# Revit family: KFL2
name_source: partatom
category: Lighting Fixtures
revit_build: Autodesk Revit 2014 (Build: 20130308_1515(x64)
units: mm (PartAtom-declared; Revit-internal decimal feet)

## types (1)
- KFL2-11L-35-RGBWW-MF-UNV-K-WH-DMX-WM
    Apparent Load = 35 VA
    Application = Flood Lighting,Sign Lighting,Landscape Lighting,Facade Lighting,Flag Pole Lighting,Sculpture Lighting,Monuments Lighting,Grazing Lighting,Washing Lighting,Column Lighting,Canopy Lighting
    Assembly Code = D5020200
    Beam Spread = Medium Flood
    Certifications = UL 1598, UL8750(LED Lightin), IP66 certified.
    Color Filter = 16777215
    Connector Description = Lighting Connector
    Control Options = DMX
    Default Elevation = 48 "
    Description = The Kim Architectural Flood is a striking timeless form that seamlessly blends high performance optics, controls, scalability and architectural mounting options which cover a wide variety of applications and enhance their environment. RGBW floods adds drama and theatricality to the site.
    Dimming Lamp Color Temperature Shift = <None>
    Features = Color Temperatures: Red, Green, Blue, White (5700K) and Red, Green, Blue, Warm White (2700K).
 Yoke and Threaded Knuckle mounting options.
  IP66 sealed optical and driver chamber.  
7 beam distributions for applications including Narrow Spot 7°x7°, Spot 10°x10°, Narrow 24°x24°, Medium 39°x38°, Medium Flood 51°x44°, Horizontal 39°x8°, and Vertical 8°x39°
    Housing Material = Paint - Hubbell - Matte White
    LED_Config = KL : 11L
    Lamp = LED
    Length = 26.38 "
    Load Classification = Lighting
    Manufacturer = Kim Lighting
    Model = KFL2
    Mounting = Threaded Krnuckle
    Mounting Accessories = Wall or Ceiling Mount
    Photometric Note = For more ies file please find the above Photometric Web Link
    Photometric Web File = KFL2-11L-35-RGBW-MF.ies
    Photometric Web Link = https://www.hubbell.com
    Power Factor = 1
    Product Doucmentation Link = https://hubbellcdn.com
    Product Page URL = https://www.hubbell.com
    Reflector Finish = Hubbell - White Glass
    Tilt Angle = 0.00°
    URL = https://www.hubbell.com
    Voltage = Universal (120-277V)
    Warranty = 5 years Warranty
    Wattage Comments = 35W
    Watts = 35 W
    Width = 11.63 "
    Width 1 = 5 "

## geometry (parser evidence)
native form markers: Blend x19, Sweep x2
no freeform markers — native parametric forms only
